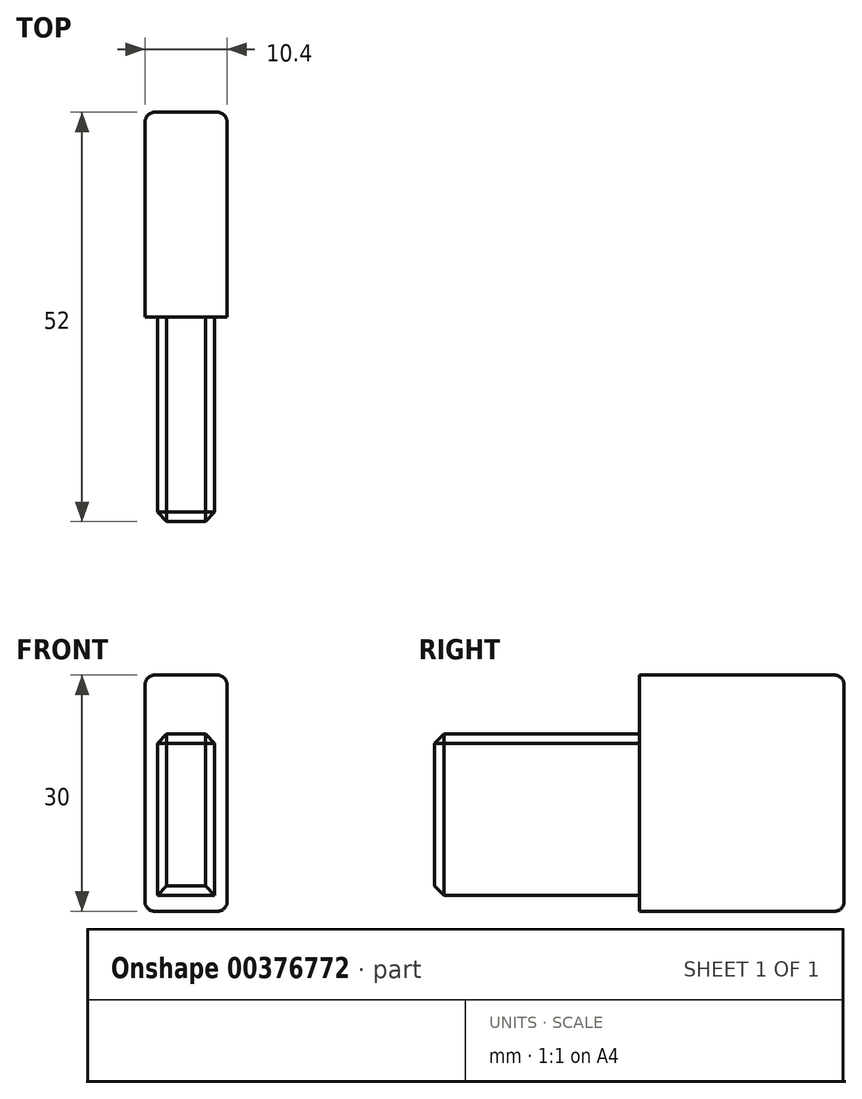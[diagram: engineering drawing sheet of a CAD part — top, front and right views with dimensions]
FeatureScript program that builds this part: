
annotation { "Feature Type Name" : "Feature", "Feature Type Description" : "" }
export const myFeature = defineFeature(function(context is Context, id is Id, definition is map)
    precondition{}
    {
        {
            var Q0;
            Q0=qCreatedBy(makeId("Right.planeOp"),FACE);
            var sketch = newSketch(context, id + "F0", { "sketchPlane" : qUnion([Q0])});
            skLineSegment(sketch, "E0.bottom", {"start": v(0, 0) * mm, "end": v(26, 0) * mm});
            skLineSegment(sketch, "E0.top", {"start": v(0, 30) * mm, "end": v(26, 30) * mm});
            skLineSegment(sketch, "E0.left", {"start": v(0, 0) * mm, "end": v(0, 30) * mm});
            skLineSegment(sketch, "E0.right", {"start": v(26, 0) * mm, "end": v(26, 30) * mm});
            skLineSegment(sketch, "E1.right", {"start": v(0, 28) * mm, "end": v(0, 7.5) * mm});
            skSolve(sketch);
        }
        {
            var Q0;
            {var subQ3=sQuery(id+"F0.wireOp",EDGE,"E0.bottom");Q0=makeQuery(id+"F0.imprint","IMPRINT",FACE,{"disambiguationData":[TD([[makeQuery(id+"F0.imprint","IMPRINT",EDGE,{"derivedFrom":subQ3}),1.0]])]});}
            extrude(context, id + "F1", {"entities" : qUnion([Q0]), "depth" : 10.4 * mm, "offsetDistance" : 25 * mm});
        }
        {
            var Q0;
            Q0=makeQuery(id+"F1.opExtrude","SWEPT_FACE",FACE,{"disambiguationData":[OSD([sQuery(id+"F0.wireOp",EDGE,"E0.left"),sQuery(id+"F0.wireOp",EDGE,"E1.right")])]});
            var sketch = newSketch(context, id + "F2", { "sketchPlane" : qUnion([Q0])});
            skLineSegment(sketch, "E2", {"start": v(5.2, 30) * mm, "end": v(5.2, 0) * mm, "construction": true});
            skLineSegment(sketch, "E3.bottom", {"start": v(8.85, 2) * mm, "end": v(1.55, 2) * mm});
            skLineSegment(sketch, "E3.top", {"start": v(8.85, 22.5) * mm, "end": v(1.55, 22.5) * mm});
            skLineSegment(sketch, "E3.left", {"start": v(8.85, 2) * mm, "end": v(8.85, 22.5) * mm});
            skLineSegment(sketch, "E3.right", {"start": v(1.55, 2) * mm, "end": v(1.55, 22.5) * mm});
            skPoint(sketch, "E3.middle", {"position": v(5.2, 12.25) * mm});
            skSolve(sketch);
        }
        {
            var Q0;
            Q0=qSketchRegion(id+"F2",true);
            extrude(context, id + "F3", {"entities" : qUnion([Q0]), "operationType" : NewBodyOperationType.ADD, "depth" : 26 * mm, "offsetDistance" : 25 * mm});
        }
        {
            var Q0;
            Q0=makeQuery(id+"F1.opExtrude","SWEPT_FACE",FACE,{"disambiguationData":[OSD([sQuery(id+"F0.wireOp",EDGE,"E0.right")])]});
            var Q1;
            Q1=makeQuery(id+"F1.opExtrude","CAP_EDGE",EDGE,{"disambiguationData":[OSD([sQuery(id+"F0.wireOp",EDGE,"E0.bottom")])],"isStart":true});
            var Q2;
            Q2=makeQuery(id+"F1.opExtrude","CAP_EDGE",EDGE,{"disambiguationData":[OSD([sQuery(id+"F0.wireOp",EDGE,"E0.bottom")])],"isStart":false});
            var Q3;
            Q3=makeQuery(id+"F1.opExtrude","CAP_EDGE",EDGE,{"disambiguationData":[OSD([sQuery(id+"F0.wireOp",EDGE,"E0.top")])],"isStart":true});
            var Q4;
            Q4=makeQuery(id+"F1.opExtrude","CAP_EDGE",EDGE,{"disambiguationData":[OSD([sQuery(id+"F0.wireOp",EDGE,"E0.top")])],"isStart":false});
            fillet(context, id + "F4", {"entities" : qUnion([Q0, Q1, Q2, Q3, Q4]), "radius" : 1.2 * mm, "tangentPropagation" : true, "allowEdgeOverflow" : false});
        }
        {
            var Q0;
            Q0=makeQuery(id+"F3.opExtrude","CAP_EDGE",EDGE,{"disambiguationData":[OSD([sQuery(id+"F2.wireOp",EDGE,"E3.right")])],"isStart":false});
            var Q1;
            Q1=makeQuery(id+"F3.opExtrude","CAP_EDGE",EDGE,{"disambiguationData":[OSD([sQuery(id+"F2.wireOp",EDGE,"E3.left")])],"isStart":false});
            var Q2;
            Q2=makeQuery(id+"F3.opExtrude","SWEPT_EDGE",EDGE,{"disambiguationData":[OSD([sQuery(id+"F2.wireOp",EDGE,"E3.top"),sQuery(id+"F2.wireOp",EDGE,"E3.left")])]});
            var Q3;
            Q3=makeQuery(id+"F3.opExtrude","SWEPT_EDGE",EDGE,{"disambiguationData":[OSD([sQuery(id+"F2.wireOp",EDGE,"E3.top"),sQuery(id+"F2.wireOp",EDGE,"E3.right")])]});
            var Q4;
            Q4=makeQuery(id+"F3.opExtrude","CAP_EDGE",EDGE,{"disambiguationData":[OSD([sQuery(id+"F2.wireOp",EDGE,"E3.top")])],"isStart":false});
            var Q5;
            Q5=makeQuery(id+"F3.opExtrude","CAP_EDGE",EDGE,{"disambiguationData":[OSD([sQuery(id+"F2.wireOp",EDGE,"E3.bottom")])],"isStart":false});
            chamfer(context, id + "F5", {"entities" : qUnion([Q0, Q1, Q2, Q3, Q4, Q5]), "width" : 1.2 * mm, "tangentPropagation" : true});
        }
    });
